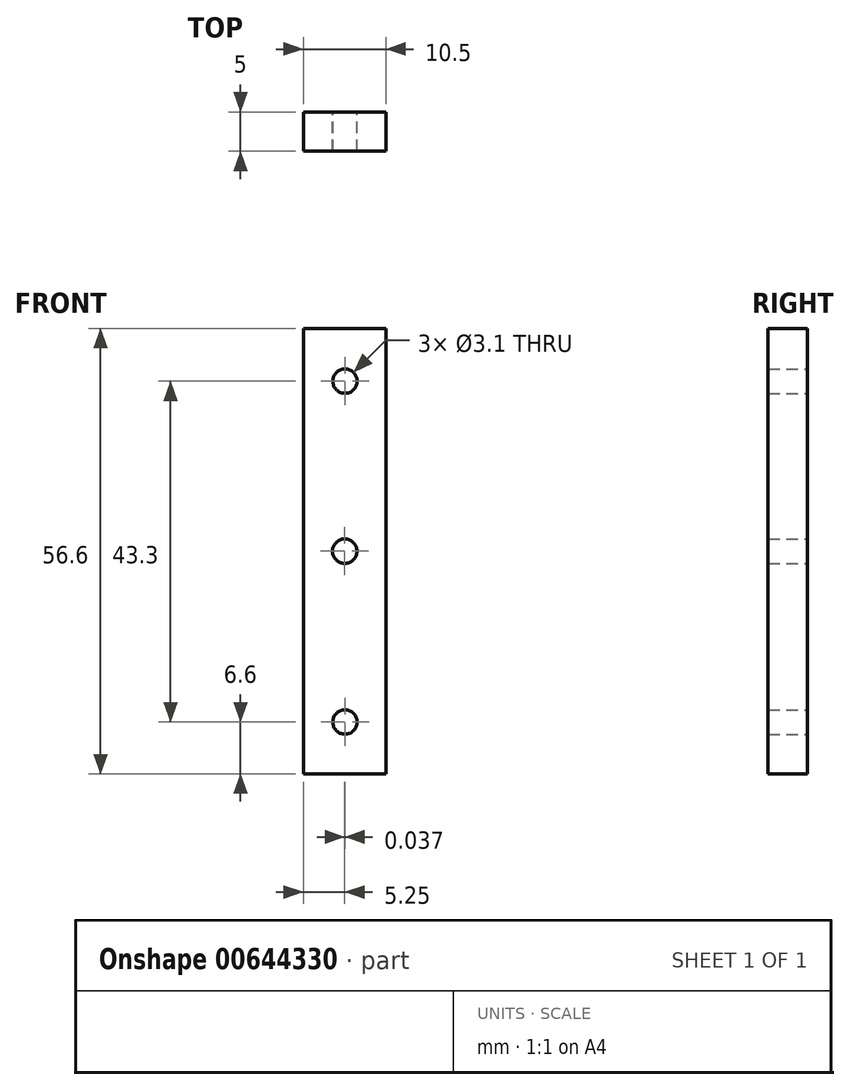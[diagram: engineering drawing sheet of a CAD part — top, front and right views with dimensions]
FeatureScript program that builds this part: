
annotation { "Feature Type Name" : "Feature", "Feature Type Description" : "" }
export const myFeature = defineFeature(function(context is Context, id is Id, definition is map)
    precondition{}
    {
        {
            var Q0;
            Q0=qCreatedBy(makeId("Front.planeOp"),FACE);
            var sketch = newSketch(context, id + "F0", { "sketchPlane" : qUnion([Q0])});
            skCircle(sketch, "E0", {"center": v(0.04, 21.6) * mm, "radius": 4 * mm, "construction": true});
            skCircle(sketch, "E1", {"center": v(0.04, -21.7) * mm, "radius": 4 * mm, "construction": true});
            skLineSegment(sketch, "E2.bottom", {"start": v(-2.62, 12.6) * mm, "end": v(2.7, 12.6) * mm, "construction": true});
            skLineSegment(sketch, "E2.top", {"start": v(-2.62, -12.4) * mm, "end": v(2.7, -12.4) * mm, "construction": true});
            skLineSegment(sketch, "E2.left", {"start": v(-2.62, 12.6) * mm, "end": v(-2.62, -12.4) * mm, "construction": true});
            skLineSegment(sketch, "E2.right", {"start": v(2.7, 12.6) * mm, "end": v(2.7, -12.4) * mm, "construction": true});
            skLineSegment(sketch, "E3.bottom", {"start": v(-5.25, 28.3) * mm, "end": v(5.25, 28.3) * mm});
            skLineSegment(sketch, "E3.top", {"start": v(-5.25, -28.3) * mm, "end": v(5.25, -28.3) * mm});
            skLineSegment(sketch, "E3.left", {"start": v(-5.25, 28.3) * mm, "end": v(-5.25, -28.3) * mm});
            skLineSegment(sketch, "E3.right", {"start": v(5.25, 28.3) * mm, "end": v(5.25, -28.3) * mm});
            skPoint(sketch, "E3.middle", {"position": v(0, 0) * mm});
            skCircle(sketch, "E4", {"center": v(0.04, 21.6) * mm, "radius": 1.55 * mm});
            skCircle(sketch, "E5", {"center": v(0.04, -21.7) * mm, "radius": 1.55 * mm});
            skCircle(sketch, "E6", {"center": v(0, 0) * mm, "radius": 1.55 * mm});
            skSolve(sketch);
        }
        {
            var Q0;
            Q0 = qSketchRegion(id + "F0", true);
            extrude(context, id + "F1", {"entities" : qUnion([Q0]), "depth" : 5 * mm, "offsetDistance" : 25 * mm});
        }
    });
